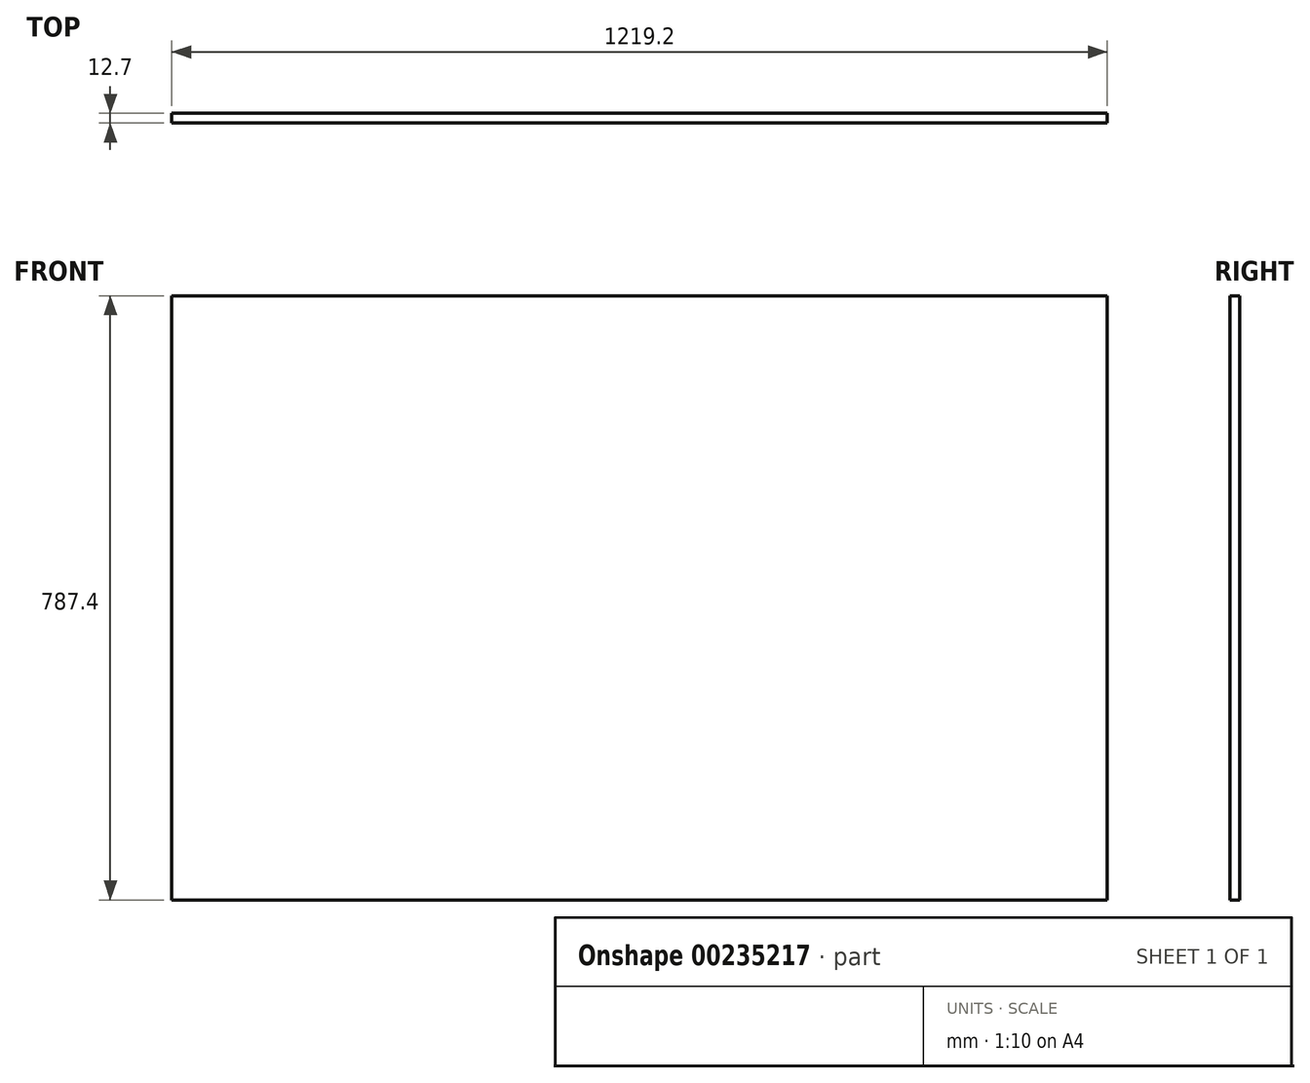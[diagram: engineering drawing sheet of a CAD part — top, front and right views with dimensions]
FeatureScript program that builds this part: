
annotation { "Feature Type Name" : "Feature", "Feature Type Description" : "" }
export const myFeature = defineFeature(function(context is Context, id is Id, definition is map)
    precondition{}
    {
        {
            var Q0;
            Q0=qCreatedBy(makeId("Front.planeOp"),FACE);
            var sketch = newSketch(context, id + "F0", { "sketchPlane" : qUnion([Q0])});
            skLineSegment(sketch, "E0.bottom", {"start": v(0, 0) * mm, "end": v(1219.2, 0) * mm});
            skLineSegment(sketch, "E0.top", {"start": v(0, -787.4) * mm, "end": v(1219.2, -787.4) * mm});
            skLineSegment(sketch, "E0.left", {"start": v(0, 0) * mm, "end": v(0, -787.4) * mm});
            skLineSegment(sketch, "E0.right", {"start": v(1219.2, 0) * mm, "end": v(1219.2, -787.4) * mm});
            skSolve(sketch);
        }
        {
            var Q0;
            Q0=makeQuery(id+"F0.imprint","IMPRINT",FACE,{"disambiguationData":[TD([[makeQuery(id+"F0.imprint","IMPRINT",EDGE,{"derivedFrom":sQuery(id+"F0.wireOp",EDGE,"E0.bottom")}),-1.0]])]});
            extrude(context, id + "F1", {"entities" : qUnion([Q0]), "depth" : 12.7 * mm});
        }
        {
            var Q0;
            Q0=makeQuery(id+"F1.opExtrude","CAP_FACE",FACE,{"disambiguationData":[OSD([sQuery(id+"F0.wireOp",EDGE,"E0.bottom"),sQuery(id+"F0.wireOp",EDGE,"E0.top"),sQuery(id+"F0.wireOp",EDGE,"E0.left"),sQuery(id+"F0.wireOp",EDGE,"E0.right")])],"isStart":false});
            var sketch = newSketch(context, id + "F2", { "sketchPlane" : qUnion([Q0])});
            skLineSegment(sketch, "E1.bottom", {"start": v(165.1, -660.4) * mm, "end": v(469.9, -660.4) * mm});
            skLineSegment(sketch, "E1.top", {"start": v(165.1, -584.2) * mm, "end": v(469.9, -584.2) * mm});
            skLineSegment(sketch, "E1.left", {"start": v(127, -622.3) * mm, "end": v(127, -622.3) * mm});
            skLineSegment(sketch, "E1.right", {"start": v(508, -622.3) * mm, "end": v(508, -622.3) * mm});
            skLineSegment(sketch, "E2", {"start": v(609.6, 0) * mm, "end": v(609.6, -787.4) * mm, "construction": true});
            skLineSegment(sketch, "E3.bottom", {"start": v(165.1, -355.6) * mm, "end": v(469.9, -355.6) * mm});
            skLineSegment(sketch, "E3.top", {"start": v(165.1, -508) * mm, "end": v(469.9, -508) * mm});
            skLineSegment(sketch, "E3.left", {"start": v(127, -393.7) * mm, "end": v(127, -469.9) * mm});
            skLineSegment(sketch, "E3.right", {"start": v(508, -393.7) * mm, "end": v(508, -469.9) * mm});
            skLineSegment(sketch, "E4.bottom", {"start": v(165.1, -127) * mm, "end": v(469.9, -127) * mm});
            skLineSegment(sketch, "E4.top", {"start": v(165.1, -279.4) * mm, "end": v(469.9, -279.4) * mm});
            skLineSegment(sketch, "E4.left", {"start": v(127, -165.1) * mm, "end": v(127, -241.3) * mm});
            skLineSegment(sketch, "E4.right", {"start": v(508, -165.1) * mm, "end": v(508, -241.3) * mm});
            skPoint(sketch, "E5.visualSharp", {"position": v(127, -127) * mm});
            skArc(sketch, "E5.filletArc", {"start": v(165.1, -127) * mm, "mid": v(138.16, -138.16) * mm, "end": v(127, -165.1) * mm});
            skPoint(sketch, "E6.visualSharp", {"position": v(127, -279.4) * mm});
            skArc(sketch, "E6.filletArc", {"start": v(127, -241.3) * mm, "mid": v(138.16, -268.24) * mm, "end": v(165.1, -279.4) * mm});
            skPoint(sketch, "E7.visualSharp", {"position": v(508, -279.4) * mm});
            skArc(sketch, "E7.filletArc", {"start": v(469.9, -279.4) * mm, "mid": v(496.84, -268.24) * mm, "end": v(508, -241.3) * mm});
            skPoint(sketch, "E8.visualSharp", {"position": v(508, -127) * mm});
            skArc(sketch, "E8.filletArc", {"start": v(508, -165.1) * mm, "mid": v(496.84, -138.16) * mm, "end": v(469.9, -127) * mm});
            skPoint(sketch, "E9.visualSharp", {"position": v(127, -355.6) * mm});
            skArc(sketch, "E9.filletArc", {"start": v(165.1, -355.6) * mm, "mid": v(138.16, -366.76) * mm, "end": v(127, -393.7) * mm});
            skPoint(sketch, "E10.visualSharp", {"position": v(127, -508) * mm});
            skArc(sketch, "E10.filletArc", {"start": v(127, -469.9) * mm, "mid": v(138.16, -496.84) * mm, "end": v(165.1, -508) * mm});
            skPoint(sketch, "E11.visualSharp", {"position": v(508, -508) * mm});
            skArc(sketch, "E11.filletArc", {"start": v(469.9, -508) * mm, "mid": v(496.84, -496.84) * mm, "end": v(508, -469.9) * mm});
            skPoint(sketch, "E12.visualSharp", {"position": v(508, -355.6) * mm});
            skArc(sketch, "E12.filletArc", {"start": v(508, -393.7) * mm, "mid": v(496.84, -366.76) * mm, "end": v(469.9, -355.6) * mm});
            skPoint(sketch, "E13.visualSharp", {"position": v(127, -584.2) * mm});
            skArc(sketch, "E13.filletArc", {"start": v(165.1, -584.2) * mm, "mid": v(138.16, -595.36) * mm, "end": v(127, -622.3) * mm});
            skPoint(sketch, "E14.visualSharp", {"position": v(508, -584.2) * mm});
            skArc(sketch, "E14.filletArc", {"start": v(508, -622.3) * mm, "mid": v(496.84, -595.36) * mm, "end": v(469.9, -584.2) * mm});
            skPoint(sketch, "E15.visualSharp", {"position": v(508, -660.4) * mm});
            skArc(sketch, "E15.filletArc", {"start": v(469.9, -660.4) * mm, "mid": v(496.84, -649.24) * mm, "end": v(508, -622.3) * mm});
            skPoint(sketch, "E16.visualSharp", {"position": v(127, -660.4) * mm});
            skArc(sketch, "E16.filletArc", {"start": v(127, -622.3) * mm, "mid": v(138.16, -649.24) * mm, "end": v(165.1, -660.4) * mm});
            skLineSegment(sketch, "E17.MirrorCS", {"start": v(711.2, -165.1) * mm, "end": v(711.2, -241.3) * mm});
            skLineSegment(sketch, "E18.MirrorCS", {"start": v(1092.2, -165.1) * mm, "end": v(1092.2, -241.3) * mm});
            skArc(sketch, "E19.MirrorCS", {"start": v(711.2, -165.1) * mm, "mid": v(722.36, -138.16) * mm, "end": v(749.3, -127) * mm});
            skPoint(sketch, "E20.MirrorP", {"position": v(711.2, -508) * mm});
            skArc(sketch, "E21.MirrorCS", {"start": v(711.2, -393.7) * mm, "mid": v(722.36, -366.76) * mm, "end": v(749.3, -355.6) * mm});
            skLineSegment(sketch, "E22.MirrorCS", {"start": v(1054.1, -660.4) * mm, "end": v(749.3, -660.4) * mm});
            skLineSegment(sketch, "E23.MirrorCS", {"start": v(1054.1, -584.2) * mm, "end": v(749.3, -584.2) * mm});
            skArc(sketch, "E24.MirrorCS", {"start": v(749.3, -279.4) * mm, "mid": v(722.36, -268.24) * mm, "end": v(711.2, -241.3) * mm});
            skArc(sketch, "E25.MirrorCS", {"start": v(1092.2, -469.9) * mm, "mid": v(1081.04, -496.84) * mm, "end": v(1054.1, -508) * mm});
            skLineSegment(sketch, "E26.MirrorCS", {"start": v(1092.2, -622.3) * mm, "end": v(1092.2, -622.3) * mm});
            skArc(sketch, "E27.MirrorCS", {"start": v(1092.2, -241.3) * mm, "mid": v(1081.04, -268.24) * mm, "end": v(1054.1, -279.4) * mm});
            skArc(sketch, "E28.MirrorCS", {"start": v(1054.1, -127) * mm, "mid": v(1081.04, -138.16) * mm, "end": v(1092.2, -165.1) * mm});
            skLineSegment(sketch, "E29.MirrorCS", {"start": v(711.2, -622.3) * mm, "end": v(711.2, -622.3) * mm});
            skArc(sketch, "E30.MirrorCS", {"start": v(749.3, -660.4) * mm, "mid": v(722.36, -649.24) * mm, "end": v(711.2, -622.3) * mm});
            skPoint(sketch, "E31.MirrorP", {"position": v(711.2, -355.6) * mm});
            skArc(sketch, "E32.MirrorCS", {"start": v(711.2, -622.3) * mm, "mid": v(722.36, -595.36) * mm, "end": v(749.3, -584.2) * mm});
            skPoint(sketch, "E33.MirrorP", {"position": v(1092.2, -127) * mm});
            skPoint(sketch, "E34.MirrorP", {"position": v(1092.2, -279.4) * mm});
            skPoint(sketch, "E35.MirrorP", {"position": v(711.2, -584.2) * mm});
            skLineSegment(sketch, "E36.MirrorCS", {"start": v(1054.1, -355.6) * mm, "end": v(749.3, -355.6) * mm});
            skArc(sketch, "E37.MirrorCS", {"start": v(1092.2, -622.3) * mm, "mid": v(1081.04, -649.24) * mm, "end": v(1054.1, -660.4) * mm});
            skArc(sketch, "E38.MirrorCS", {"start": v(1054.1, -584.2) * mm, "mid": v(1081.04, -595.36) * mm, "end": v(1092.2, -622.3) * mm});
            skLineSegment(sketch, "E39.MirrorCS", {"start": v(1092.2, -393.7) * mm, "end": v(1092.2, -469.9) * mm});
            skLineSegment(sketch, "E40.MirrorCS", {"start": v(711.2, -393.7) * mm, "end": v(711.2, -469.9) * mm});
            skPoint(sketch, "E41.MirrorP", {"position": v(1092.2, -355.6) * mm});
            skPoint(sketch, "E42.MirrorP", {"position": v(1092.2, -584.2) * mm});
            skPoint(sketch, "E43.MirrorP", {"position": v(711.2, -279.4) * mm});
            skPoint(sketch, "E44.MirrorP", {"position": v(711.2, -660.4) * mm});
            skLineSegment(sketch, "E45.MirrorCS", {"start": v(1054.1, -508) * mm, "end": v(749.3, -508) * mm});
            skPoint(sketch, "E46.MirrorP", {"position": v(1092.2, -660.4) * mm});
            skLineSegment(sketch, "E47.MirrorCS", {"start": v(1054.1, -127) * mm, "end": v(749.3, -127) * mm});
            skArc(sketch, "E48.MirrorCS", {"start": v(749.3, -508) * mm, "mid": v(722.36, -496.84) * mm, "end": v(711.2, -469.9) * mm});
            skPoint(sketch, "E49.MirrorP", {"position": v(711.2, -127) * mm});
            skPoint(sketch, "E50.MirrorP", {"position": v(1092.2, -508) * mm});
            skArc(sketch, "E51.MirrorCS", {"start": v(1054.1, -355.6) * mm, "mid": v(1081.04, -366.76) * mm, "end": v(1092.2, -393.7) * mm});
            skLineSegment(sketch, "E52.MirrorCS", {"start": v(1054.1, -279.4) * mm, "end": v(749.3, -279.4) * mm});
            skSolve(sketch);
        }
        {
            var Q0;
            Q0=makeQuery(id+"F1.opExtrude","SWEPT_BODY",BODY,{"disambiguationData":[OSD([sQuery(id+"F0.wireOp",EDGE,"E0.bottom"),sQuery(id+"F0.wireOp",EDGE,"E0.top"),sQuery(id+"F0.wireOp",EDGE,"E0.left"),sQuery(id+"F0.wireOp",EDGE,"E0.right")])]});
            transform(context, id + "F3", {"entities" : qUnion([Q0]), "transformType" : TransformType.TRANSLATION_3D, "dx" : 0 * mm, "dy" : 0 * mm, "dz" : 0 * mm, "makeCopy" : true});
        }
        {
            var Q0;
            Q0=makeQuery(id+"F3.opPattern","COPY",BODY,{"derivedFrom":makeQuery(id+"F1.opExtrude","SWEPT_BODY",BODY,{"disambiguationData":[OSD([sQuery(id+"F0.wireOp",EDGE,"E0.bottom"),sQuery(id+"F0.wireOp",EDGE,"E0.top"),sQuery(id+"F0.wireOp",EDGE,"E0.left"),sQuery(id+"F0.wireOp",EDGE,"E0.right")])]}),"instanceName":"1"});
            deleteBodies(context, id + "F4", {"entities" : qUnion([Q0])});
        }
    });
